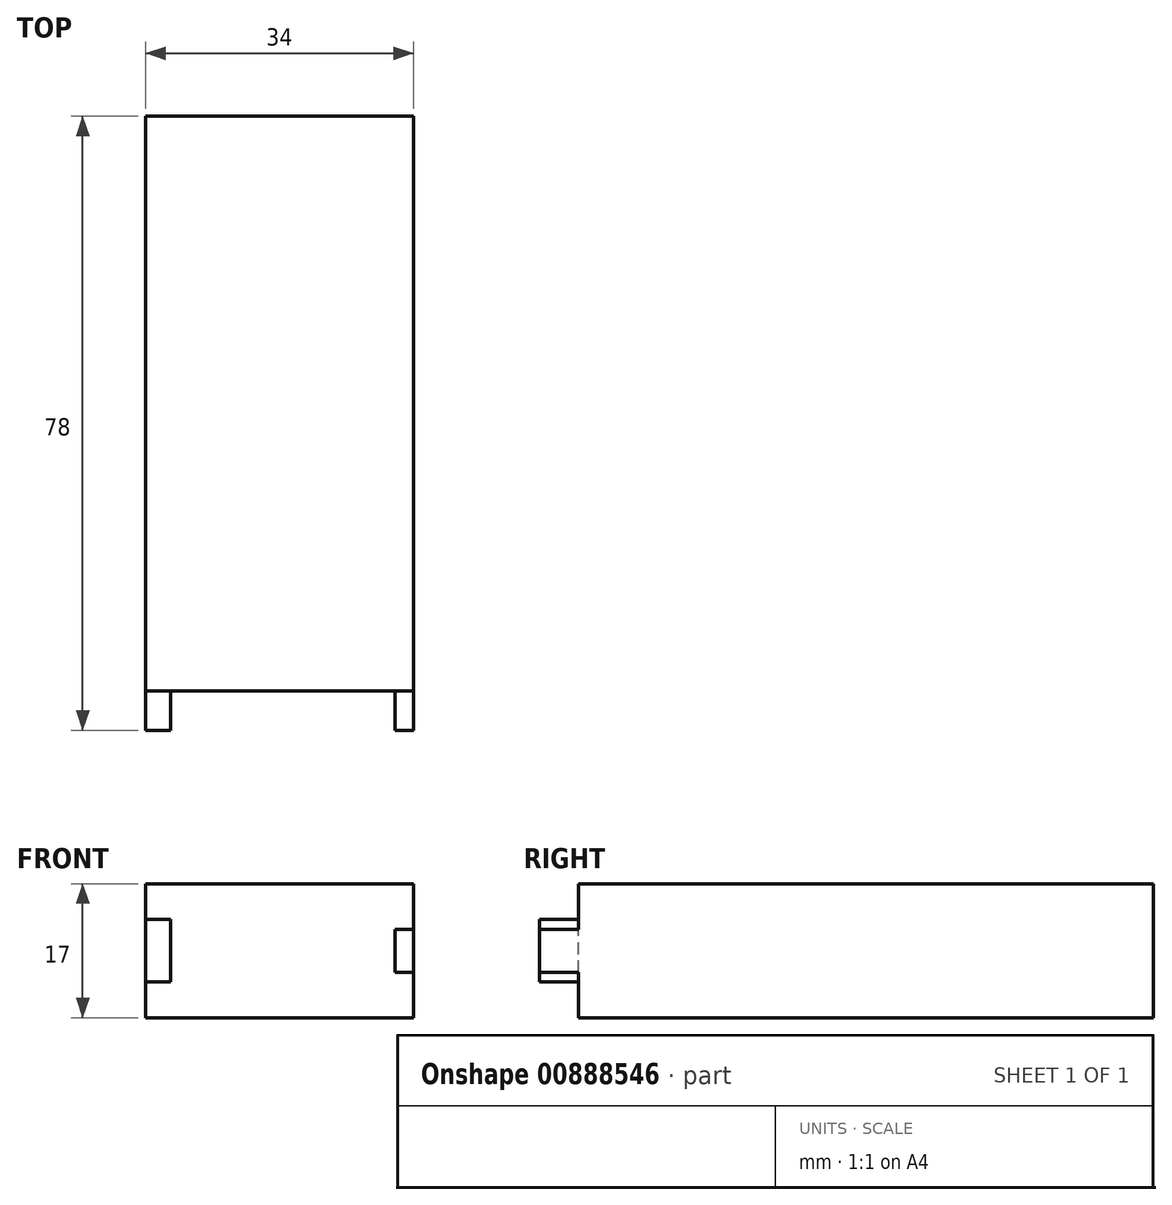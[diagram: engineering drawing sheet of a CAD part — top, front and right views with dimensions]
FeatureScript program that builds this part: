
annotation { "Feature Type Name" : "Feature", "Feature Type Description" : "" }
export const myFeature = defineFeature(function(context is Context, id is Id, definition is map)
    precondition{}
    {
        {
            var Q0;
            Q0=qCreatedBy(makeId("Top.planeOp"),FACE);
            var sketch = newSketch(context, id + "F0", { "sketchPlane" : qUnion([Q0])});
            skLineSegment(sketch, "E0.bottom", {"start": v(-17, -36.5) * mm, "end": v(17, -36.5) * mm});
            skLineSegment(sketch, "E0.top", {"start": v(-17, 36.5) * mm, "end": v(17, 36.5) * mm});
            skLineSegment(sketch, "E0.left", {"start": v(-17, -36.5) * mm, "end": v(-17, 36.5) * mm});
            skLineSegment(sketch, "E0.right", {"start": v(17, -36.5) * mm, "end": v(17, 36.5) * mm});
            skPoint(sketch, "E0.middle", {"position": v(0, 0) * mm});
            skSolve(sketch);
        }
        {
            var Q0;
            Q0 = qSketchRegion(id + "F0", true);
            extrude(context, id + "F1", {"entities" : qUnion([Q0]), "depth" : 17 * mm, "offsetDistance" : 25 * mm});
        }
        {
            var Q0;
            Q0=makeQuery(id+"F1.opExtrude","SWEPT_FACE",FACE,{"disambiguationData":[OSD([sQuery(id+"F0.wireOp",EDGE,"E0.bottom")])]});
            var sketch = newSketch(context, id + "F2", { "sketchPlane" : qUnion([Q0])});
            skLineSegment(sketch, "E1.bottom", {"start": v(-13.86, 4.53) * mm, "end": v(-17, 4.53) * mm});
            skLineSegment(sketch, "E1.top", {"start": v(-13.86, 12.47) * mm, "end": v(-17, 12.47) * mm});
            skLineSegment(sketch, "E1.left", {"start": v(-13.86, 4.53) * mm, "end": v(-13.86, 12.47) * mm});
            skLineSegment(sketch, "E1.right", {"start": v(-17, 4.53) * mm, "end": v(-17, 12.47) * mm});
            skPoint(sketch, "E1.middle", {"position": v(-15.43, 8.5) * mm});
            skLineSegment(sketch, "E2.bottom", {"start": v(17, 5.77) * mm, "end": v(14.68, 5.77) * mm});
            skLineSegment(sketch, "E2.top", {"start": v(17, 11.23) * mm, "end": v(14.68, 11.23) * mm});
            skLineSegment(sketch, "E2.left", {"start": v(17, 5.77) * mm, "end": v(17, 11.23) * mm});
            skLineSegment(sketch, "E2.right", {"start": v(14.68, 5.77) * mm, "end": v(14.68, 11.23) * mm});
            skPoint(sketch, "E2.middle", {"position": v(15.84, 8.5) * mm});
            skSolve(sketch);
        }
        {
            var Q0;
            Q0 = qSketchRegion(id + "F2", true);
            extrude(context, id + "F3", {"entities" : qUnion([Q0]), "operationType" : NewBodyOperationType.ADD, "depth" : 5 * mm, "offsetDistance" : 25 * mm});
        }
    });
